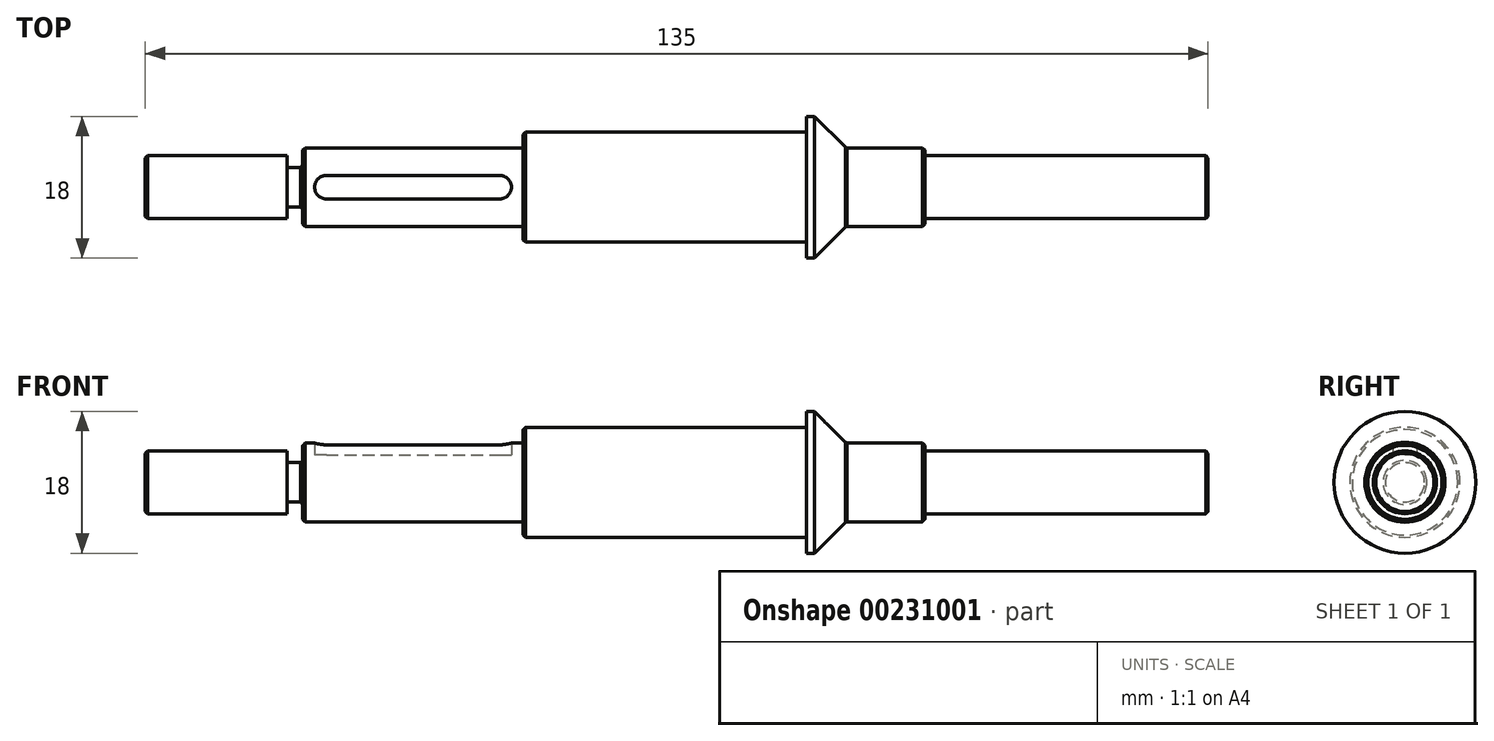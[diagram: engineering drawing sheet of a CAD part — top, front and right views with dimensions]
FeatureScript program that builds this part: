
annotation { "Feature Type Name" : "Feature", "Feature Type Description" : "" }
export const myFeature = defineFeature(function(context is Context, id is Id, definition is map)
    precondition{}
    {
        {
            var Q0;
            Q0=qCreatedBy(makeId("Front.planeOp"),FACE);
            var sketch = newSketch(context, id + "F0", { "sketchPlane" : qUnion([Q0])});
            skLineSegment(sketch, "E0", {"start": v(0, 0) * mm, "end": v(0, 4) * mm});
            skLineSegment(sketch, "E1", {"start": v(0, 4) * mm, "end": v(18, 4) * mm});
            skLineSegment(sketch, "E2", {"start": v(18, 4) * mm, "end": v(18, 2.5) * mm});
            skLineSegment(sketch, "E3", {"start": v(18, 2.5) * mm, "end": v(20, 2.5) * mm});
            skLineSegment(sketch, "E4", {"start": v(20, 2.5) * mm, "end": v(20, 5) * mm});
            skLineSegment(sketch, "E5", {"start": v(20, 5) * mm, "end": v(48, 5) * mm});
            skLineSegment(sketch, "E6", {"start": v(48, 5) * mm, "end": v(48, 7) * mm});
            skLineSegment(sketch, "E7", {"start": v(48, 7) * mm, "end": v(84, 7) * mm});
            skLineSegment(sketch, "E8", {"start": v(84, 7) * mm, "end": v(84, 9) * mm});
            skLineSegment(sketch, "E9", {"start": v(84, 9) * mm, "end": v(85, 9) * mm});
            skLineSegment(sketch, "E10", {"start": v(85, 9) * mm, "end": v(89, 5) * mm});
            skLineSegment(sketch, "E11", {"start": v(89, 5) * mm, "end": v(99, 5) * mm});
            skLineSegment(sketch, "E12", {"start": v(99, 5) * mm, "end": v(99, 4) * mm});
            skLineSegment(sketch, "E13", {"start": v(99, 4) * mm, "end": v(135, 4) * mm});
            skLineSegment(sketch, "E14", {"start": v(135, 4) * mm, "end": v(135, 0) * mm});
            skLineSegment(sketch, "E15", {"start": v(135, 0) * mm, "end": v(0, 0) * mm});
            skLineSegment(sketch, "E16", {"start": v(99, 5) * mm, "end": v(99, 0) * mm});
            skLineSegment(sketch, "E17", {"start": v(84, 9) * mm, "end": v(84, 0) * mm});
            skLineSegment(sketch, "E18", {"start": v(20, 5) * mm, "end": v(23, 5) * mm});
            skLineSegment(sketch, "E19", {"start": v(23, 5) * mm, "end": v(45, 5) * mm});
            skLineSegment(sketch, "E20", {"start": v(45, 5) * mm, "end": v(46.5, 5) * mm});
            skLineSegment(sketch, "E21", {"start": v(135, 4) * mm, "end": v(120, 4) * mm});
            skLineSegment(sketch, "E22", {"start": v(120, 4) * mm, "end": v(120, 0) * mm});
            skSolve(sketch);
        }
        {
            var Q0;
            Q0=qCreatedBy(makeId("Front.planeOp"),FACE);
            var sketch = newSketch(context, id + "F1", { "sketchPlane" : qUnion([Q0])});
            skLineSegment(sketch, "E23", {"start": v(-14.73, 0) * mm, "end": v(142.2, 0) * mm, "construction": true});
            skSolve(sketch);
        }
        {
            var Q0;
            {var subQ0=sQuery(id+"F0.wireOp",EDGE,"E0");Q0=makeQuery(id+"F0.imprint","IMPRINT",FACE,{"disambiguationData":[TD([[makeQuery(id+"F0.imprint","IMPRINT",EDGE,{"derivedFrom":subQ0}),-1.0]])]});}
            var Q1;
            {var subQ6=sQuery(id+"F0.wireOp",EDGE,"E9");Q1=makeQuery(id+"F0.imprint","IMPRINT",FACE,{"disambiguationData":[TD([[makeQuery(id+"F0.imprint","IMPRINT",EDGE,{"derivedFrom":subQ6}),-1.0]])]});}
            var Q2;
            {var subQ0=sQuery(id+"F0.wireOp",EDGE,"E13");Q2=makeQuery(id+"F0.imprint","IMPRINT",FACE,{"disambiguationData":[TD([[makeQuery(id+"F0.imprint","IMPRINT",EDGE,{"derivedFrom":subQ0}),-1.0]])]});}
            var Q3;
            Q3=sQuery(id+"F1.wireOp",EDGE,"E23");
            revolve(context, id + "F2", {"entities" : qUnion([Q0, Q1, Q2]), "axis" : qUnion([Q3]), "revolveType" : RevolveType.FULL});
        }
        {
            var Q0;
            Q0=qCreatedBy(makeId("Top.planeOp"),FACE);
            cPlane(context, id + "F3", {"entities" : qUnion([Q0]), "cplaneType" : CPlaneType.OFFSET, "offset" : 3.5 * mm, "width" : 150 * mm, "height" : 150 * mm});
        }
        {
            var Q0;
            Q0=qCreatedBy(id+"F3.planeOp",FACE);
            var sketch = newSketch(context, id + "F4", { "sketchPlane" : qUnion([Q0])});
            skLineSegment(sketch, "E24", {"start": v(19.38, 0) * mm, "end": v(21.5, 0) * mm});
            skArc(sketch, "E25", {"start": v(23, 1.5) * mm, "mid": v(21.5, 0) * mm, "end": v(23, -1.5) * mm});
            skArc(sketch, "E26", {"start": v(45, -1.5) * mm, "mid": v(46.5, 0) * mm, "end": v(45, 1.5) * mm});
            skLineSegment(sketch, "E27", {"start": v(20, 0) * mm, "end": v(20, 0.08) * mm});
            skLineSegment(sketch, "E28", {"start": v(20, 0) * mm, "end": v(21.5, 0) * mm});
            skLineSegment(sketch, "E29.top", {"start": v(23, 1.5) * mm, "end": v(45, 1.5) * mm});
            skLineSegment(sketch, "E30.top", {"start": v(23, -1.5) * mm, "end": v(45, -1.5) * mm});
            skLineSegment(sketch, "E31.trimOffspring", {"start": v(46.5, 0) * mm, "end": v(49.35, 0) * mm});
            skSolve(sketch);
        }
        {
            var Q0;
            Q0 = qSketchRegion(id + "F4", true);
            extrude(context, id + "F5", {"entities" : qUnion([Q0]), "operationType" : NewBodyOperationType.REMOVE, "endBound" : BoundingType.UP_TO_NEXT, "depth" : 3 * mm});
        }
        {
            var Q0;
            Q0=makeQuery(id+"F2.opRevolve","SWEPT_EDGE",EDGE,{"disambiguationData":[OSD([sQuery(id+"F0.wireOp",EDGE,"E13"),sQuery(id+"F0.wireOp",EDGE,"E21"),sQuery(id+"F0.wireOp",EDGE,"E22")])]});
            var Q1;
            Q1=makeQuery(id+"F2.opRevolve","SWEPT_EDGE",EDGE,{"disambiguationData":[OSD([sQuery(id+"F0.wireOp",EDGE,"E11"),sQuery(id+"F0.wireOp",EDGE,"E16")])]});
            var Q2;
            Q2=makeQuery(id+"F2.opRevolve","SWEPT_EDGE",EDGE,{"disambiguationData":[OSD([sQuery(id+"F0.wireOp",EDGE,"E6"),sQuery(id+"F0.wireOp",EDGE,"E7")])]});
            var Q3;
            Q3=makeQuery(id+"F2.opRevolve","SWEPT_EDGE",EDGE,{"disambiguationData":[OSD([sQuery(id+"F0.wireOp",EDGE,"E4"),sQuery(id+"F0.wireOp",EDGE,"E18")])]});
            var Q4;
            Q4=makeQuery(id+"F2.opRevolve","SWEPT_EDGE",EDGE,{"disambiguationData":[OSD([sQuery(id+"F0.wireOp",EDGE,"E0"),sQuery(id+"F0.wireOp",EDGE,"E1")])]});
            chamfer(context, id + "F6", {"entities" : qUnion([Q0, Q1, Q2, Q3, Q4]), "width" : 0.3 * mm, "tangentPropagation" : true});
        }
    });
